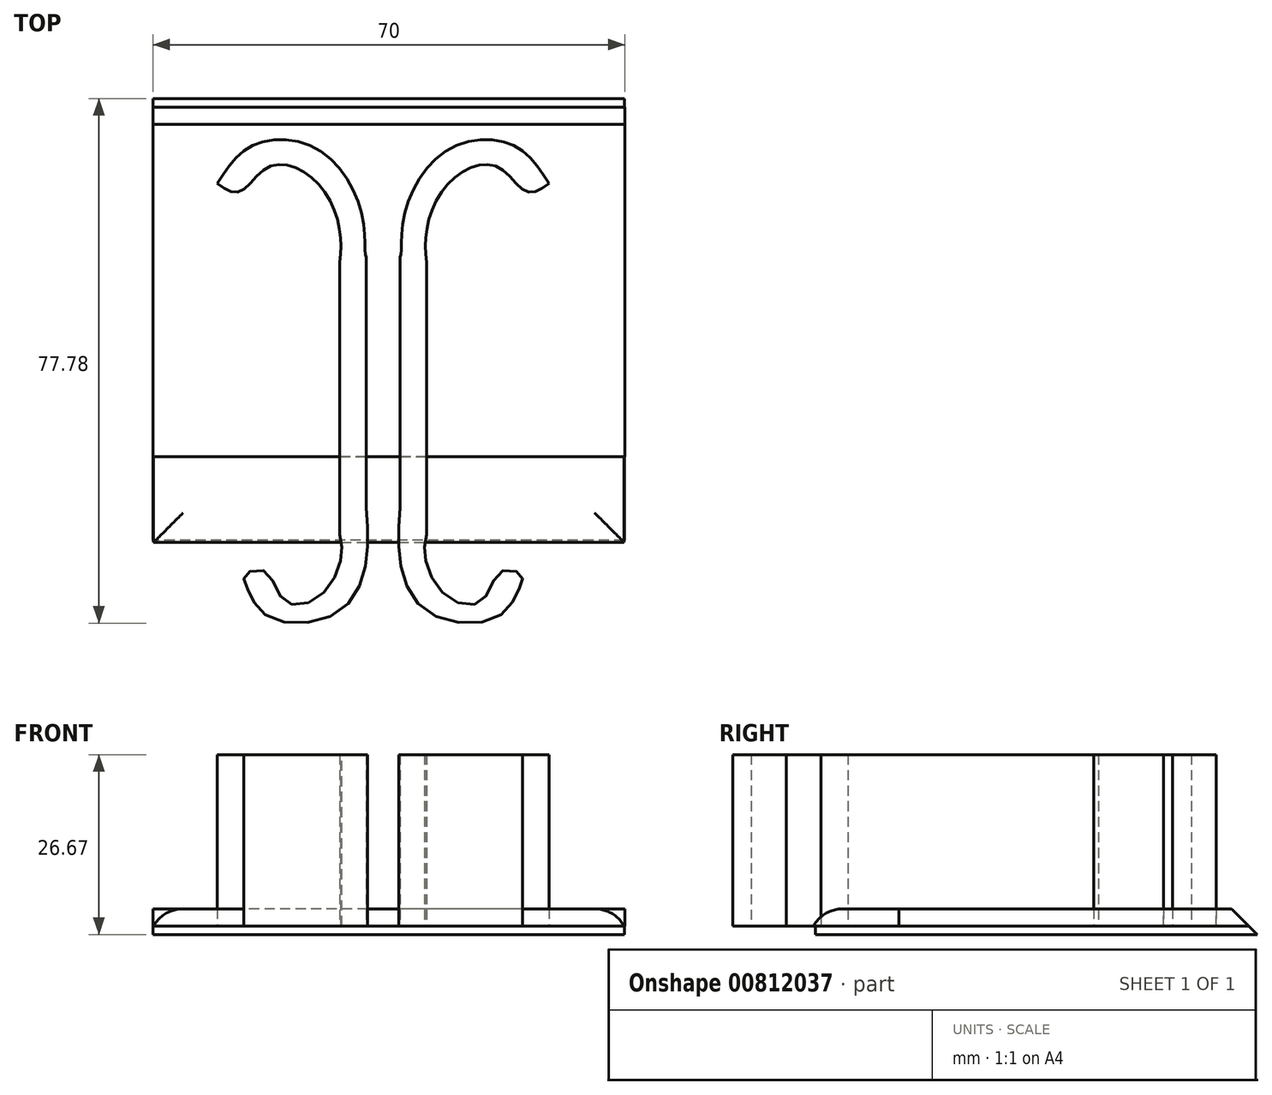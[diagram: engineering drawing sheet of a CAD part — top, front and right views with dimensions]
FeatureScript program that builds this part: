
annotation { "Feature Type Name" : "Feature", "Feature Type Description" : "" }
export const myFeature = defineFeature(function(context is Context, id is Id, definition is map)
    precondition{}
    {
        {
            var Q0;
            Q0=qCreatedBy(makeId("Top.planeOp"),FACE);
            var sketch = newSketch(context, id + "F0", { "sketchPlane" : qUnion([Q0])});
            skFitSpline(sketch, "E0", {"points": [v(-25.39, 29.17) * mm, v(-19.98, 34.85) * mm, v(-10.34, 34.1) * mm, v(-4.04, 24.85) * mm, v(-3.46, 19) * mm, v(-3.33, 18.22) * mm], "startDerivative": vector(19.91, 30.7) * mm, "endDerivative": vector(2.16, -8.52) * mm});
            skLineSegment(sketch, "E1", {"start": v(-3.33, 18.22) * mm, "end": v(-3.33, -18.94) * mm});
            skFitSpline(sketch, "E2", {"points": [v(-3.33, -18.94) * mm, v(-3.33, -26.99) * mm, v(-7.67, -34.53) * mm, v(-17.9, -35.08) * mm, v(-20.98, -30.84) * mm, v(-21.3, -28.9) * mm, v(-18.21, -28.38) * mm, v(-15.51, -32.69) * mm, v(-10.43, -32.22) * mm, v(-7.02, -26.48) * mm, v(-7.21, -22.94) * mm], "startDerivative": vector(5.43, -65.4) * mm, "endDerivative": vector(-8.04, 40.25) * mm});
            skLineSegment(sketch, "E3", {"start": v(-7.21, -22.94) * mm, "end": v(-7.21, 17.47) * mm});
            skFitSpline(sketch, "E4", {"points": [v(-7.21, 17.47) * mm, v(-7.21, 22) * mm, v(-9.5, 27.95) * mm, v(-14.18, 31.65) * mm, v(-18.46, 31.2) * mm, v(-22.12, 27.91) * mm, v(-25.39, 29.17) * mm], "startDerivative": vector(2.14, 27.1) * mm, "endDerivative": vector(-23.83, 16.79) * mm});
            skSolve(sketch);
        }
        {
            var Q0;
            Q0 = qSketchRegion(id + "F0", true);
            extrude(context, id + "F1", {"entities" : qUnion([Q0]), "depth" : 25.4 * mm, "offsetDistance" : 25.4 * mm});
        }
        {
            var Q0;
            Q0=makeQuery(id+"F1.opExtrude","SWEPT_FACE",FACE,{"disambiguationData":[OSD([sQuery(id+"F0.wireOp",EDGE,"E1")])]});
            cPlane(context, id + "F2", {"entities" : qUnion([Q0]), "cplaneType" : CPlaneType.OFFSET, "offset" : 2.54 * mm, "width" : 152.4 * mm, "height" : 152.4 * mm});
        }
        {
            var Q0;
            Q0=makeQuery(id+"F1.opExtrude","SWEPT_BODY",BODY,{"disambiguationData":[OSD([sQuery(id+"F0.wireOp",EDGE,"E0"),sQuery(id+"F0.wireOp",EDGE,"E1"),sQuery(id+"F0.wireOp",EDGE,"E2"),sQuery(id+"F0.wireOp",EDGE,"E3"),sQuery(id+"F0.wireOp",EDGE,"E4")])]});
            var Q1;
            Q1=qCreatedBy(id+"F2.planeOp",FACE);
            mirror(context, id + "F3", {"entities" : qUnion([Q0]), "mirrorPlane" : qUnion([Q1])});
        }
        {
            var Q0;
            Q0=qCreatedBy(makeId("Top.planeOp"),FACE);
            var sketch = newSketch(context, id + "F4", { "sketchPlane" : qUnion([Q0])});
            skLineSegment(sketch, "E5.bottom", {"start": v(-34.85, -24.09) * mm, "end": v(34.95, -24.09) * mm});
            skLineSegment(sketch, "E5.top", {"start": v(-34.85, -11.39) * mm, "end": v(34.95, -11.39) * mm});
            skLineSegment(sketch, "E5.left", {"start": v(-34.85, -24.09) * mm, "end": v(-34.85, -11.39) * mm});
            skLineSegment(sketch, "E5.right", {"start": v(34.95, -24.09) * mm, "end": v(34.95, -11.39) * mm});
            skSolve(sketch);
        }
        {
            var Q0;
            Q0 = qSketchRegion(id + "F4", true);
            extrude(context, id + "F5", {"entities" : qUnion([Q0]), "depth" : 2.54 * mm, "offsetDistance" : 25.4 * mm});
        }
        {
            var Q0;
            Q0=makeQuery(id+"F5.opExtrude","CAP_EDGE",EDGE,{"disambiguationData":[OSD([sQuery(id+"F4.wireOp",EDGE,"E5.bottom")])],"isStart":false});
            fillet(context, id + "F6", {"entities" : qUnion([Q0]), "radius" : 5.08 * mm, "tangentPropagation" : true, "allowEdgeOverflow" : false});
        }
        {
            var Q0;
            Q0=makeQuery(id+"F5.opExtrude","CAP_EDGE",EDGE,{"disambiguationData":[OSD([sQuery(id+"F4.wireOp",EDGE,"E5.left")])],"isStart":false});
            fillet(context, id + "F7", {"entities" : qUnion([Q0]), "radius" : 5.08 * mm, "tangentPropagation" : true, "allowEdgeOverflow" : false});
        }
        {
            var Q0;
            Q0=makeQuery(id+"F5.opExtrude","CAP_EDGE",EDGE,{"disambiguationData":[OSD([sQuery(id+"F4.wireOp",EDGE,"E5.right")])],"isStart":false});
            fillet(context, id + "F8", {"entities" : qUnion([Q0]), "radius" : 5.08 * mm, "tangentPropagation" : true, "allowEdgeOverflow" : false});
        }
        {
            var Q0;
            Q0=qCreatedBy(makeId("Top.planeOp"),FACE);
            var sketch = newSketch(context, id + "F9", { "sketchPlane" : qUnion([Q0])});
            skLineSegment(sketch, "E6.bottom", {"start": v(35.05, -11.38) * mm, "end": v(-34.95, -11.38) * mm});
            skLineSegment(sketch, "E6.top", {"start": v(35.05, 45.55) * mm, "end": v(-34.95, 45.55) * mm});
            skLineSegment(sketch, "E6.left", {"start": v(35.05, -11.38) * mm, "end": v(35.05, 45.55) * mm});
            skLineSegment(sketch, "E6.right", {"start": v(-34.95, -11.38) * mm, "end": v(-34.95, 45.55) * mm});
            skSolve(sketch);
        }
        {
            var Q0;
            Q0 = qSketchRegion(id + "F9", true);
            extrude(context, id + "F10", {"entities" : qUnion([Q0]), "depth" : 2.54 * mm, "offsetDistance" : 25.4 * mm});
        }
        {
            var Q0;
            Q0=makeQuery(id+"F10.opExtrude","CAP_FACE",FACE,{"disambiguationData":[OSD([sQuery(id+"F9.wireOp",EDGE,"E6.bottom"),sQuery(id+"F9.wireOp",EDGE,"E6.top"),sQuery(id+"F9.wireOp",EDGE,"E6.left"),sQuery(id+"F9.wireOp",EDGE,"E6.right")])],"isStart":true});
            var sketch = newSketch(context, id + "F11", { "sketchPlane" : qUnion([Q0])});
            skLineSegment(sketch, "E7.bottom", {"start": v(35, 23.78) * mm, "end": v(-34.95, 23.78) * mm});
            skLineSegment(sketch, "E7.top", {"start": v(35, -43.01) * mm, "end": v(-34.95, -43.01) * mm});
            skLineSegment(sketch, "E7.left", {"start": v(35, 23.78) * mm, "end": v(35, -43.01) * mm});
            skLineSegment(sketch, "E7.right", {"start": v(-34.95, 23.78) * mm, "end": v(-34.95, -43.01) * mm});
            skSolve(sketch);
        }
        {
            var Q0;
            Q0 = qSketchRegion(id + "F11", true);
            extrude(context, id + "F12", {"entities" : qUnion([Q0]), "depth" : 1.27 * mm, "offsetDistance" : 25.4 * mm});
        }
        {
            var Q0;
            Q0=makeQuery(id+"F10.opExtrude","CAP_EDGE",EDGE,{"disambiguationData":[OSD([sQuery(id+"F9.wireOp",EDGE,"E6.top")])],"isStart":false});
            chamfer(context, id + "F13", {"entities" : qUnion([Q0]), "width" : 7.62 * mm, "tangentPropagation" : true});
        }
        {
            var Q0;
            Q0=makeQuery(id+"F12.opExtrude","CAP_EDGE",EDGE,{"disambiguationData":[OSD([sQuery(id+"F11.wireOp",EDGE,"E7.top")])],"isStart":true});
            chamfer(context, id + "F14", {"entities" : qUnion([Q0]), "width" : 2.54 * mm, "tangentPropagation" : true});
        }
    });
